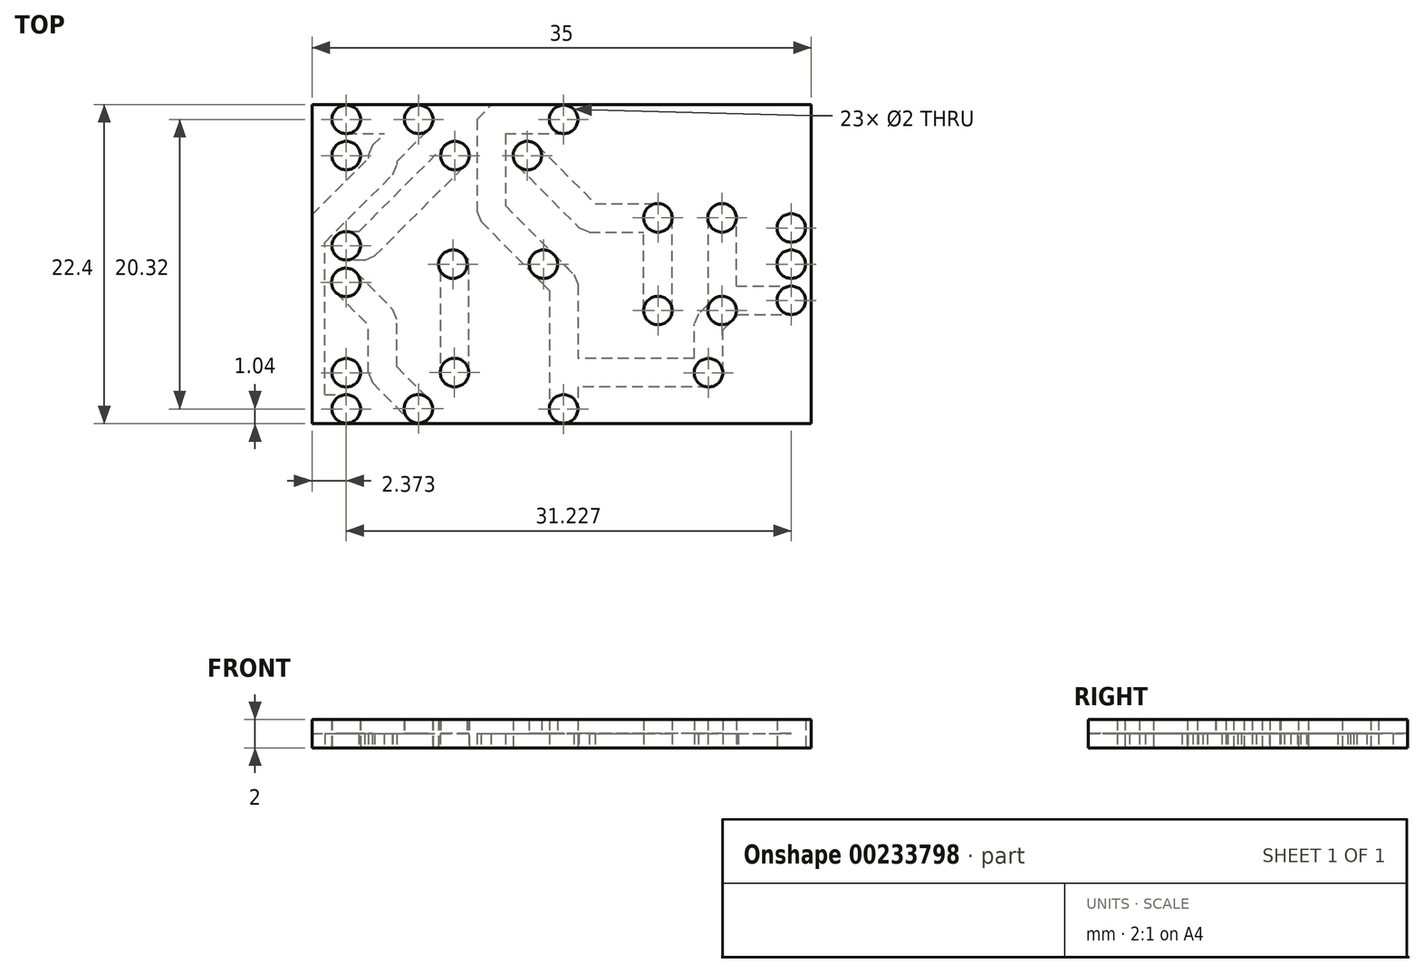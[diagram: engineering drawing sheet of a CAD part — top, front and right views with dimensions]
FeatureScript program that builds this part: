
annotation { "Feature Type Name" : "Feature", "Feature Type Description" : "" }
export const myFeature = defineFeature(function(context is Context, id is Id, definition is map)
    precondition{}
    {
        {
            var Q0;
            Q0=qCreatedBy(makeId("Top.planeOp"),FACE);
            var sketch = newSketch(context, id + "F0", { "sketchPlane" : qUnion([Q0])});
            skLineSegment(sketch, "E0.0", {"start": v(27.94, 0) * mm, "end": v(27.94, 15.24) * mm});
            skLineSegment(sketch, "E1", {"start": v(15.24, 15.24) * mm, "end": v(15.24, 17.78) * mm});
            skLineSegment(sketch, "E2.0", {"start": v(10.65, 6.33) * mm, "end": v(10.65, 8.91) * mm});
            skLineSegment(sketch, "E3.0", {"start": v(13.83, 6.33) * mm, "end": v(13.83, 8.91) * mm});
            skLineSegment(sketch, "E4.0", {"start": v(7.47, 6.33) * mm, "end": v(7.47, 8.91) * mm});
            skLineSegment(sketch, "E5.0", {"start": v(20.85, 6.33) * mm, "end": v(20.85, 8.91) * mm});
            skLineSegment(sketch, "E6.0", {"start": v(29.35, 6.33) * mm, "end": v(29.35, 8.91) * mm});
            skLineSegment(sketch, "E7.0", {"start": v(33.05, 6.33) * mm, "end": v(33.05, 8.91) * mm});
            skLineSegment(sketch, "E8.0", {"start": v(27.35, 6.33) * mm, "end": v(27.35, 8.91) * mm});
            skLineSegment(sketch, "E9", {"start": v(20.85, 7.62) * mm, "end": v(27.35, 7.62) * mm});
            skLineSegment(sketch, "E10", {"start": v(29.35, 7.62) * mm, "end": v(33.05, 7.62) * mm});
            skLineSegment(sketch, "E11", {"start": v(31.2, 7.62) * mm, "end": v(31.2, 10.16) * mm});
            skLineSegment(sketch, "E12", {"start": v(2.54, 15.24) * mm, "end": v(5.08, 17.78) * mm});
            skLineSegment(sketch, "E13", {"start": v(21.85, 4.37) * mm, "end": v(21.85, 10.87) * mm});
            skLineSegment(sketch, "E14", {"start": v(26.35, 10.87) * mm, "end": v(26.35, 4.37) * mm});
            skLineSegment(sketch, "E15", {"start": v(10.16, 17.78) * mm, "end": v(15.24, 17.78) * mm});
            skLineSegment(sketch, "E16", {"start": v(25.4, 0) * mm, "end": v(15.24, 0) * mm});
            skLineSegment(sketch, "E17", {"start": v(2.53, 0.01) * mm, "end": v(5.05, -2.53) * mm});
            skLineSegment(sketch, "E18", {"start": v(0, 15.24) * mm, "end": v(0, 8.91) * mm});
            skLineSegment(sketch, "E19", {"start": v(-2.56, -2.54) * mm, "end": v(0, -2.54) * mm});
            skLineSegment(sketch, "E20", {"start": v(0, 8.91) * mm, "end": v(0, 8.4) * mm});
            skLineSegment(sketch, "E21", {"start": v(2.54, 15.24) * mm, "end": v(2.54, 14.61) * mm});
            skLineSegment(sketch, "E22.trimOffspring", {"start": v(1.3, 8.91) * mm, "end": v(7.62, 15.24) * mm});
            skLineSegment(sketch, "E23", {"start": v(-0.03, 6.34) * mm, "end": v(2.53, 3.76) * mm});
            skLineSegment(sketch, "E24", {"start": v(2.53, 0.01) * mm, "end": v(2.53, 3.76) * mm});
            skLineSegment(sketch, "E25", {"start": v(12.7, 15.24) * mm, "end": v(17.03, 10.87) * mm});
            skLineSegment(sketch, "E26", {"start": v(17.03, 10.87) * mm, "end": v(21.85, 10.87) * mm});
            skLineSegment(sketch, "E27", {"start": v(15.24, 6.2) * mm, "end": v(15.24, -2.54) * mm});
            skLineSegment(sketch, "E28", {"start": v(25.4, 3.42) * mm, "end": v(27.06, 5.08) * mm});
            skLineSegment(sketch, "E29", {"start": v(27.06, 5.08) * mm, "end": v(31.2, 5.08) * mm});
            skLineSegment(sketch, "E30", {"start": v(1.3, 8.91) * mm, "end": v(0, 8.91) * mm});
            skLineSegment(sketch, "E31", {"start": v(-2.52, 0) * mm, "end": v(-2.52, 9.56) * mm});
            skLineSegment(sketch, "E32", {"start": v(25.4, 0) * mm, "end": v(25.4, 3.42) * mm});
            skLineSegment(sketch, "E33", {"start": v(0, 17.78) * mm, "end": v(5.08, 17.78) * mm});
            skLineSegment(sketch, "E34", {"start": v(-2.52, 9.56) * mm, "end": v(2.54, 14.61) * mm});
            skLineSegment(sketch, "E35", {"start": v(10.16, 11.32) * mm, "end": v(15.24, 6.2) * mm});
            skLineSegment(sketch, "E36", {"start": v(10.16, 17.78) * mm, "end": v(10.16, 11.32) * mm});
            skCircle(sketch, "E37", {"center": v(0, 17.78) * mm, "radius": 1 * mm});
            skCircle(sketch, "E38", {"center": v(5.08, 17.78) * mm, "radius": 1 * mm});
            skCircle(sketch, "E39", {"center": v(0, 15.24) * mm, "radius": 1 * mm});
            skCircle(sketch, "E40", {"center": v(7.62, 15.24) * mm, "radius": 1 * mm});
            skCircle(sketch, "E41", {"center": v(0, 8.91) * mm, "radius": 1 * mm});
            skCircle(sketch, "E42", {"center": v(-0.03, 6.34) * mm, "radius": 1 * mm});
            skCircle(sketch, "E43", {"center": v(0, 0) * mm, "radius": 1 * mm});
            skCircle(sketch, "E44", {"center": v(0, -2.54) * mm, "radius": 1 * mm});
            skCircle(sketch, "E45", {"center": v(5.05, -2.53) * mm, "radius": 1 * mm});
            skCircle(sketch, "E46", {"center": v(15.24, 17.78) * mm, "radius": 1 * mm});
            skCircle(sketch, "E47", {"center": v(12.7, 15.24) * mm, "radius": 1 * mm});
            skCircle(sketch, "E48", {"center": v(21.85, 10.87) * mm, "radius": 1 * mm});
            skCircle(sketch, "E49", {"center": v(21.85, 4.37) * mm, "radius": 1 * mm});
            skCircle(sketch, "E50", {"center": v(13.83, 7.62) * mm, "radius": 1 * mm});
            skCircle(sketch, "E51", {"center": v(26.35, 10.87) * mm, "radius": 1 * mm});
            skCircle(sketch, "E52", {"center": v(26.35, 4.37) * mm, "radius": 1 * mm});
            skCircle(sketch, "E53", {"center": v(25.4, 0) * mm, "radius": 1 * mm});
            skCircle(sketch, "E54", {"center": v(15.24, -2.54) * mm, "radius": 1 * mm});
            skCircle(sketch, "E55", {"center": v(31.2, 5.08) * mm, "radius": 1 * mm});
            skCircle(sketch, "E56", {"center": v(31.2, 7.62) * mm, "radius": 1 * mm});
            skCircle(sketch, "E57", {"center": v(31.2, 10.16) * mm, "radius": 1 * mm});
            skLineSegment(sketch, "E58.0", {"start": v(0, 16.78) * mm, "end": v(5.08, 16.78) * mm});
            skLineSegment(sketch, "E59.0", {"start": v(0, 18.78) * mm, "end": v(5.08, 18.78) * mm});
            skLineSegment(sketch, "E60.0", {"start": v(3.25, 14.53) * mm, "end": v(5.79, 17.07) * mm});
            skLineSegment(sketch, "E61.0", {"start": v(1.83, 15.95) * mm, "end": v(4.37, 18.49) * mm});
            skLineSegment(sketch, "E62.0", {"start": v(1.54, 15.24) * mm, "end": v(1.54, 14.61) * mm});
            skLineSegment(sketch, "E63.0", {"start": v(3.54, 15.24) * mm, "end": v(3.54, 14.61) * mm});
            skLineSegment(sketch, "E64.0", {"start": v(-1.81, 8.85) * mm, "end": v(3.25, 13.9) * mm});
            skLineSegment(sketch, "E65.0", {"start": v(-3.23, 10.26) * mm, "end": v(1.83, 15.32) * mm});
            skLineSegment(sketch, "E66.0", {"start": v(-1.52, 0) * mm, "end": v(-1.52, 9.56) * mm});
            skLineSegment(sketch, "E67.0", {"start": v(2, 8.2) * mm, "end": v(8.33, 14.53) * mm});
            skLineSegment(sketch, "E68.0", {"start": v(0.58, 9.62) * mm, "end": v(6.91, 15.95) * mm});
            skLineSegment(sketch, "E69.0", {"start": v(1.3, 7.9) * mm, "end": v(0, 7.9) * mm});
            skLineSegment(sketch, "E70.0", {"start": v(1.3, 9.91) * mm, "end": v(0, 9.91) * mm});
            skLineSegment(sketch, "E71.0", {"start": v(3.55, 0.98) * mm, "end": v(1.03, 3.52) * mm});
            skLineSegment(sketch, "E72", {"start": v(0, -2.54) * mm, "end": v(-2.52, -2.54) * mm});
            skLineSegment(sketch, "E73", {"start": v(-2.52, -2.54) * mm, "end": v(-2.52, 0) * mm});
            skLineSegment(sketch, "E74.0", {"start": v(-2.52, -3.54) * mm, "end": v(0, -3.54) * mm});
            skLineSegment(sketch, "E75.0", {"start": v(-2.56, -1.54) * mm, "end": v(0, -1.54) * mm});
            skLineSegment(sketch, "E76", {"start": v(-1.52, 0) * mm, "end": v(-1.52, -1.54) * mm});
            skLineSegment(sketch, "E77", {"start": v(-2.52, -2.54) * mm, "end": v(-2.52, -3.54) * mm});
            skLineSegment(sketch, "E78.0", {"start": v(-0.74, 5.64) * mm, "end": v(1.82, 3.06) * mm});
            skLineSegment(sketch, "E79.0", {"start": v(0.68, 7.05) * mm, "end": v(3.24, 4.47) * mm});
            skLineSegment(sketch, "E80.0", {"start": v(3.53, 0.01) * mm, "end": v(3.53, 3.77) * mm});
            skLineSegment(sketch, "E81.0", {"start": v(1.53, 0) * mm, "end": v(1.53, 3.76) * mm});
            skCircle(sketch, "E82", {"center": v(7.6, 0.01) * mm, "radius": 1 * mm});
            skCircle(sketch, "E83", {"center": v(7.47, 7.62) * mm, "radius": 1 * mm});
            skLineSegment(sketch, "E84.0", {"start": v(1.82, -0.7) * mm, "end": v(4.34, -3.23) * mm});
            skLineSegment(sketch, "E85.0", {"start": v(3.24, 0.72) * mm, "end": v(5.76, -1.82) * mm});
            skLineSegment(sketch, "E86", {"start": v(6.6, 7.15) * mm, "end": v(6.6, 0.01) * mm});
            skLineSegment(sketch, "E87", {"start": v(7.47, 7.62) * mm, "end": v(5.78, 5.92) * mm});
            skLineSegment(sketch, "E88", {"start": v(5.78, 5.92) * mm, "end": v(8.47, 8.61) * mm});
            skLineSegment(sketch, "E89", {"start": v(8.18, 8.33) * mm, "end": v(8.9, 7.62) * mm});
            skLineSegment(sketch, "E90", {"start": v(8.6, 0) * mm, "end": v(8.6, 7.92) * mm});
            skLineSegment(sketch, "E91.0", {"start": v(10.16, 16.78) * mm, "end": v(15.24, 16.78) * mm});
            skLineSegment(sketch, "E92.0", {"start": v(10.16, 18.78) * mm, "end": v(15.24, 18.78) * mm});
            skLineSegment(sketch, "E93.0", {"start": v(11.16, 17.78) * mm, "end": v(11.16, 11.32) * mm});
            skLineSegment(sketch, "E94.0", {"start": v(9.16, 17.78) * mm, "end": v(9.16, 11.32) * mm});
            skLineSegment(sketch, "E95.0", {"start": v(9.45, 10.61) * mm, "end": v(14.53, 5.49) * mm});
            skLineSegment(sketch, "E96.0", {"start": v(10.87, 12.02) * mm, "end": v(15.95, 6.9) * mm});
            skLineSegment(sketch, "E97.0", {"start": v(13.4, 15.94) * mm, "end": v(17.74, 11.57) * mm});
            skLineSegment(sketch, "E98.0", {"start": v(12, 14.54) * mm, "end": v(16.32, 10.17) * mm});
            skLineSegment(sketch, "E99.0", {"start": v(17.03, 9.87) * mm, "end": v(21.85, 9.87) * mm});
            skLineSegment(sketch, "E100.0", {"start": v(17.03, 11.87) * mm, "end": v(21.85, 11.87) * mm});
            skLineSegment(sketch, "E101.0", {"start": v(14.24, 6.2) * mm, "end": v(14.24, -2.54) * mm});
            skLineSegment(sketch, "E102.0", {"start": v(16.24, 6.2) * mm, "end": v(16.24, -2.54) * mm});
            skLineSegment(sketch, "E103.0", {"start": v(22.85, 4.37) * mm, "end": v(22.85, 10.87) * mm});
            skLineSegment(sketch, "E104.0", {"start": v(20.85, 4.37) * mm, "end": v(20.85, 10.87) * mm});
            skLineSegment(sketch, "E105.0", {"start": v(25.35, 10.87) * mm, "end": v(25.35, 4.37) * mm});
            skLineSegment(sketch, "E106.0", {"start": v(27.35, 10.87) * mm, "end": v(27.35, 4.37) * mm});
            skLineSegment(sketch, "E107.0", {"start": v(27.06, 4.08) * mm, "end": v(31.2, 4.08) * mm});
            skLineSegment(sketch, "E108.0", {"start": v(27.06, 6.08) * mm, "end": v(31.2, 6.08) * mm});
            skLineSegment(sketch, "E109.0", {"start": v(26.4, 0) * mm, "end": v(26.4, 3.42) * mm});
            skLineSegment(sketch, "E110.0", {"start": v(24.4, 0) * mm, "end": v(24.4, 3.42) * mm});
            skLineSegment(sketch, "E111.0", {"start": v(25.64, 5.08) * mm, "end": v(24.7, 4.13) * mm});
            skLineSegment(sketch, "E112.0", {"start": v(26.1, 2.71) * mm, "end": v(27.77, 4.37) * mm});
            skLineSegment(sketch, "E113", {"start": v(24.7, 4.13) * mm, "end": v(24.4, 3.42) * mm});
            skLineSegment(sketch, "E114", {"start": v(17.03, 9.87) * mm, "end": v(16.32, 10.17) * mm});
            skLineSegment(sketch, "E115", {"start": v(15.95, 6.9) * mm, "end": v(16.24, 6.2) * mm});
            skLineSegment(sketch, "E116", {"start": v(9.16, 11.32) * mm, "end": v(9.45, 10.61) * mm});
            skLineSegment(sketch, "E117", {"start": v(9.16, 17.78) * mm, "end": v(10.16, 18.78) * mm});
            skLineSegment(sketch, "E118", {"start": v(3.24, 4.47) * mm, "end": v(3.53, 3.77) * mm});
            skLineSegment(sketch, "E119", {"start": v(1.53, 0) * mm, "end": v(1.82, -0.7) * mm});
            skLineSegment(sketch, "E120", {"start": v(1.3, 7.9) * mm, "end": v(2, 8.2) * mm});
            skLineSegment(sketch, "E121", {"start": v(3.25, 13.9) * mm, "end": v(3.54, 14.61) * mm});
            skLineSegment(sketch, "E122", {"start": v(1.83, 15.95) * mm, "end": v(1.54, 15.24) * mm});
            skLineSegment(sketch, "E123", {"start": v(-2.52, 9.56) * mm, "end": v(-2.52, 10.97) * mm});
            skLineSegment(sketch, "E124.0", {"start": v(25.4, 1) * mm, "end": v(15.24, 1) * mm});
            skLineSegment(sketch, "E125.0", {"start": v(25.4, -1) * mm, "end": v(15.24, -1) * mm});
            skSolve(sketch);
        }
        {
            var Q0;
            Q0=qCreatedBy(makeId("Top.planeOp"),FACE);
            var sketch = newSketch(context, id + "F1", { "sketchPlane" : qUnion([Q0])});
            skLineSegment(sketch, "E126", {"start": v(-2.4, -4.38) * mm, "end": v(-2.4, 19.62) * mm});
            skLineSegment(sketch, "E127", {"start": v(-2.4, 19.62) * mm, "end": v(32.6, 19.62) * mm});
            skLineSegment(sketch, "E128", {"start": v(32.6, 19.62) * mm, "end": v(32.6, -4.38) * mm});
            skLineSegment(sketch, "E129", {"start": v(32.6, -4.38) * mm, "end": v(-2.4, -4.38) * mm});
            skLineSegment(sketch, "E130.0", {"start": v(32.6, -3.58) * mm, "end": v(-2.4, -3.58) * mm});
            skLineSegment(sketch, "E131.0", {"start": v(-2.4, 18.82) * mm, "end": v(32.6, 18.82) * mm});
            skSolve(sketch);
        }
        {
            var Q0;
            {var subQ0=sQuery(id+"F1.wireOp",EDGE,"E130.0");Q0=makeQuery(id+"F1.imprint","IMPRINT",FACE,{"disambiguationData":[TD([[makeQuery(id+"F1.imprint","IMPRINT",EDGE,{"derivedFrom":subQ0}),-1.0]])]});}
            extrude(context, id + "F2", {"entities" : qUnion([Q0]), "depth" : 2 * mm});
        }
        {
            var Q0;
            Q0 = qSketchRegion(id + "F0", true);
            var Q1;
            {var subQ0=sQuery(id+"F0.wireOp",EDGE,"E61.0");var subQ1=sQuery(id+"F0.wireOp",EDGE,"E33");var subQ2=makeQuery(id+"F0.imprint","INTERSECT",VERTEX,{"derivedFrom":[subQ1,subQ0]});Q1=makeQuery(id+"F0.imprint","IMPRINT",FACE,{"disambiguationData":[TD([[makeQuery(id+"F0.imprint","IMPRINT",EDGE,{"disambiguationData":[TD([[subQ2,-1.0]])],"derivedFrom":subQ1}),1.0]])]});}
            var Q2;
            {var subQ0=sQuery(id+"F0.wireOp",EDGE,"E33");var subQ1=sQuery(id+"F0.wireOp",EDGE,"E12");var subQ2=makeQuery(id+"F0.imprint","INTERSECT",VERTEX,{"derivedFrom":[subQ1,subQ0]});Q2=makeQuery(id+"F0.imprint","IMPRINT",FACE,{"disambiguationData":[TD([[makeQuery(id+"F0.imprint","IMPRINT",EDGE,{"disambiguationData":[TD([[subQ2,1.0]])],"derivedFrom":subQ1}),1.0]])]});}
            var Q3;
            {var subQ0=sQuery(id+"F0.wireOp",EDGE,"E58.0");var subQ1=sQuery(id+"F0.wireOp",EDGE,"E12");var subQ2=makeQuery(id+"F0.imprint","INTERSECT",VERTEX,{"derivedFrom":[subQ1,subQ0]});Q3=makeQuery(id+"F0.imprint","IMPRINT",FACE,{"disambiguationData":[TD([[makeQuery(id+"F0.imprint","IMPRINT",EDGE,{"disambiguationData":[TD([[subQ2,-1.0]])],"derivedFrom":subQ1}),-1.0]])]});}
            var Q4;
            {var subQ0=sQuery(id+"F0.wireOp",EDGE,"E83");var subQ1=sQuery(id+"F0.wireOp",EDGE,"E4.0");var subQ2=makeQuery(id+"F0.imprint","INTERSECT",VERTEX,{"disambiguationData":[OD(1.0)],"derivedFrom":[subQ1,subQ0]});Q4=makeQuery(id+"F0.imprint","IMPRINT",FACE,{"disambiguationData":[TD([[makeQuery(id+"F0.imprint","IMPRINT",EDGE,{"disambiguationData":[TD([[subQ2,-1.0]])],"derivedFrom":subQ1}),1.0]])]});}
            var Q5;
            {var subQ0=sQuery(id+"F0.wireOp",EDGE,"E50");var subQ1=sQuery(id+"F0.wireOp",EDGE,"E3.0");var subQ2=makeQuery(id+"F0.imprint","INTERSECT",VERTEX,{"disambiguationData":[OD(1.0)],"derivedFrom":[subQ1,subQ0]});Q5=makeQuery(id+"F0.imprint","IMPRINT",FACE,{"disambiguationData":[TD([[makeQuery(id+"F0.imprint","IMPRINT",EDGE,{"disambiguationData":[TD([[subQ2,1.0]])],"derivedFrom":subQ1}),1.0]])]});}
            var Q6;
            {var subQ0=sQuery(id+"F0.wireOp",EDGE,"E50");var subQ1=sQuery(id+"F0.wireOp",EDGE,"E3.0");var subQ2=makeQuery(id+"F0.imprint","INTERSECT",VERTEX,{"disambiguationData":[OD(0.0)],"derivedFrom":[subQ1,subQ0]});Q6=makeQuery(id+"F0.imprint","IMPRINT",FACE,{"disambiguationData":[TD([[makeQuery(id+"F0.imprint","IMPRINT",EDGE,{"disambiguationData":[TD([[subQ2,-1.0]])],"derivedFrom":subQ1}),-1.0]])]});}
            var Q7;
            {var subQ0=sQuery(id+"F0.wireOp",EDGE,"E26");var subQ1=sQuery(id+"F0.wireOp",EDGE,"E13");var subQ2=makeQuery(id+"F0.imprint","INTERSECT",VERTEX,{"derivedFrom":[subQ1,subQ0]});Q7=makeQuery(id+"F0.imprint","IMPRINT",FACE,{"disambiguationData":[TD([[makeQuery(id+"F0.imprint","IMPRINT",EDGE,{"disambiguationData":[TD([[subQ2,1.0]])],"derivedFrom":subQ1}),1.0]])]});}
            var Q8;
            {var subQ2=sQuery(id+"F0.wireOp",EDGE,"E14");var subQ4=sQuery(id+"F0.wireOp",EDGE,"E28");var subQ5=makeQuery(id+"F0.imprint","INTERSECT",VERTEX,{"derivedFrom":[subQ2,subQ4]});Q8=makeQuery(id+"F0.imprint","IMPRINT",FACE,{"disambiguationData":[TD([[makeQuery(id+"F0.imprint","IMPRINT",EDGE,{"disambiguationData":[TD([[subQ5,1.0]])],"derivedFrom":subQ2}),-1.0]])]});}
            var Q9;
            {var subQ0=sQuery(id+"F0.wireOp",EDGE,"E28");var subQ1=sQuery(id+"F0.wireOp",EDGE,"E14");var subQ2=makeQuery(id+"F0.imprint","INTERSECT",VERTEX,{"derivedFrom":[subQ1,subQ0]});Q9=makeQuery(id+"F0.imprint","IMPRINT",FACE,{"disambiguationData":[TD([[makeQuery(id+"F0.imprint","IMPRINT",EDGE,{"disambiguationData":[TD([[subQ2,1.0]])],"derivedFrom":subQ1}),1.0]])]});}
            var Q10;
            {var subQ0=sQuery(id+"F0.wireOp",EDGE,"E29");var subQ1=sQuery(id+"F0.wireOp",EDGE,"E28");var subQ2=makeQuery(id+"F0.imprint","INTERSECT",VERTEX,{"derivedFrom":[subQ1,subQ0]});Q10=makeQuery(id+"F0.imprint","IMPRINT",FACE,{"disambiguationData":[TD([[makeQuery(id+"F0.imprint","IMPRINT",EDGE,{"disambiguationData":[TD([[subQ2,1.0]])],"derivedFrom":subQ1}),-1.0]])]});}
            extrude(context, id + "F3", {"entities" : qUnion([Q0, Q1, Q2, Q3, Q4, Q5, Q6, Q7, Q8, Q9, Q10]), "operationType" : NewBodyOperationType.REMOVE, "depth" : 1 * mm});
        }
        {
            var Q0;
            {var subQ0=sQuery(id+"F0.wireOp",EDGE,"E15");var subQ1=sQuery(id+"F0.wireOp",EDGE,"E1");var subQ2=makeQuery(id+"F0.imprint","INTERSECT",VERTEX,{"derivedFrom":[subQ1,subQ0]});Q0=makeQuery(id+"F0.imprint","IMPRINT",FACE,{"disambiguationData":[TD([[makeQuery(id+"F0.imprint","IMPRINT",EDGE,{"disambiguationData":[TD([[subQ2,1.0]])],"derivedFrom":subQ0}),1.0]])]});}
            var Q1;
            {var subQ0=sQuery(id+"F0.wireOp",EDGE,"E15");var subQ1=sQuery(id+"F0.wireOp",EDGE,"E1");var subQ2=makeQuery(id+"F0.imprint","INTERSECT",VERTEX,{"derivedFrom":[subQ1,subQ0]});Q1=makeQuery(id+"F0.imprint","IMPRINT",FACE,{"disambiguationData":[TD([[makeQuery(id+"F0.imprint","IMPRINT",EDGE,{"disambiguationData":[TD([[subQ2,1.0]])],"derivedFrom":subQ0}),-1.0]])]});}
            var Q2;
            {var subQ0=sQuery(id+"F0.wireOp",EDGE,"E47");var subQ1=makeQuery(id+"F0.imprint","INTERSECT",VERTEX,{"derivedFrom":[subQ0,sQuery(id+"F0.wireOp",EDGE,"E97.0")]});Q2=makeQuery(id+"F0.imprint","IMPRINT",FACE,{"disambiguationData":[TD([[makeQuery(id+"F0.imprint","IMPRINT",EDGE,{"disambiguationData":[TD([[subQ1,-1.0]])],"derivedFrom":subQ0}),1.0]])]});}
            var Q3;
            {var subQ0=sQuery(id+"F0.wireOp",EDGE,"E50");var subQ1=sQuery(id+"F0.wireOp",EDGE,"E3.0");var subQ2=makeQuery(id+"F0.imprint","INTERSECT",VERTEX,{"disambiguationData":[OD(1.0)],"derivedFrom":[subQ1,subQ0]});Q3=makeQuery(id+"F0.imprint","IMPRINT",FACE,{"disambiguationData":[TD([[makeQuery(id+"F0.imprint","IMPRINT",EDGE,{"disambiguationData":[TD([[subQ2,1.0]])],"derivedFrom":subQ1}),-1.0]])]});}
            var Q4;
            {var subQ0=sQuery(id+"F0.wireOp",EDGE,"E50");var subQ1=sQuery(id+"F0.wireOp",EDGE,"E3.0");var subQ2=makeQuery(id+"F0.imprint","INTERSECT",VERTEX,{"disambiguationData":[OD(1.0)],"derivedFrom":[subQ1,subQ0]});Q4=makeQuery(id+"F0.imprint","IMPRINT",FACE,{"disambiguationData":[TD([[makeQuery(id+"F0.imprint","IMPRINT",EDGE,{"disambiguationData":[TD([[subQ2,1.0]])],"derivedFrom":subQ1}),1.0]])]});}
            var Q5;
            {var subQ0=sQuery(id+"F0.wireOp",EDGE,"E50");var subQ1=sQuery(id+"F0.wireOp",EDGE,"E3.0");var subQ2=makeQuery(id+"F0.imprint","INTERSECT",VERTEX,{"disambiguationData":[OD(0.0)],"derivedFrom":[subQ1,subQ0]});Q5=makeQuery(id+"F0.imprint","IMPRINT",FACE,{"disambiguationData":[TD([[makeQuery(id+"F0.imprint","IMPRINT",EDGE,{"disambiguationData":[TD([[subQ2,-1.0]])],"derivedFrom":subQ1}),-1.0]])]});}
            var Q6;
            {var subQ0=sQuery(id+"F0.wireOp",EDGE,"E50");var subQ1=sQuery(id+"F0.wireOp",EDGE,"E3.0");var subQ2=makeQuery(id+"F0.imprint","INTERSECT",VERTEX,{"disambiguationData":[OD(0.0)],"derivedFrom":[subQ1,subQ0]});Q6=makeQuery(id+"F0.imprint","IMPRINT",FACE,{"disambiguationData":[TD([[makeQuery(id+"F0.imprint","IMPRINT",EDGE,{"disambiguationData":[TD([[subQ2,-1.0]])],"derivedFrom":subQ1}),1.0]])]});}
            var Q7;
            {var subQ0=sQuery(id+"F0.wireOp",EDGE,"E83");var subQ1=sQuery(id+"F0.wireOp",EDGE,"E4.0");var subQ2=makeQuery(id+"F0.imprint","INTERSECT",VERTEX,{"disambiguationData":[OD(1.0)],"derivedFrom":[subQ1,subQ0]});Q7=makeQuery(id+"F0.imprint","IMPRINT",FACE,{"disambiguationData":[TD([[makeQuery(id+"F0.imprint","IMPRINT",EDGE,{"disambiguationData":[TD([[subQ2,-1.0]])],"derivedFrom":subQ1}),-1.0]])]});}
            var Q8;
            {var subQ0=sQuery(id+"F0.wireOp",EDGE,"E83");var subQ1=sQuery(id+"F0.wireOp",EDGE,"E4.0");var subQ2=makeQuery(id+"F0.imprint","INTERSECT",VERTEX,{"disambiguationData":[OD(0.0)],"derivedFrom":[subQ1,subQ0]});Q8=makeQuery(id+"F0.imprint","IMPRINT",FACE,{"disambiguationData":[TD([[makeQuery(id+"F0.imprint","IMPRINT",EDGE,{"disambiguationData":[TD([[subQ2,1.0]])],"derivedFrom":subQ1}),-1.0]])]});}
            var Q9;
            {var subQ0=sQuery(id+"F0.wireOp",EDGE,"E83");var subQ1=sQuery(id+"F0.wireOp",EDGE,"E4.0");var subQ2=makeQuery(id+"F0.imprint","INTERSECT",VERTEX,{"disambiguationData":[OD(0.0)],"derivedFrom":[subQ1,subQ0]});Q9=makeQuery(id+"F0.imprint","IMPRINT",FACE,{"disambiguationData":[TD([[makeQuery(id+"F0.imprint","IMPRINT",EDGE,{"disambiguationData":[TD([[subQ2,1.0]])],"derivedFrom":subQ1}),1.0]])]});}
            var Q10;
            {var subQ0=sQuery(id+"F0.wireOp",EDGE,"E83");var subQ1=sQuery(id+"F0.wireOp",EDGE,"E4.0");var subQ2=makeQuery(id+"F0.imprint","INTERSECT",VERTEX,{"disambiguationData":[OD(1.0)],"derivedFrom":[subQ1,subQ0]});Q10=makeQuery(id+"F0.imprint","IMPRINT",FACE,{"disambiguationData":[TD([[makeQuery(id+"F0.imprint","IMPRINT",EDGE,{"disambiguationData":[TD([[subQ2,-1.0]])],"derivedFrom":subQ1}),1.0]])]});}
            var Q11;
            {var subQ0=sQuery(id+"F0.wireOp",EDGE,"E82");var subQ1=makeQuery(id+"F0.imprint","INTERSECT",VERTEX,{"derivedFrom":[subQ0,sQuery(id+"F0.wireOp",EDGE,"E86")]});Q11=makeQuery(id+"F0.imprint","IMPRINT",FACE,{"disambiguationData":[TD([[makeQuery(id+"F0.imprint","IMPRINT",EDGE,{"disambiguationData":[TD([[subQ1,1.0]])],"derivedFrom":subQ0}),1.0]])]});}
            var Q12;
            {var subQ0=sQuery(id+"F0.wireOp",EDGE,"E42");var subQ1=makeQuery(id+"F0.imprint","INTERSECT",VERTEX,{"derivedFrom":[subQ0,sQuery(id+"F0.wireOp",EDGE,"E78.0")]});Q12=makeQuery(id+"F0.imprint","IMPRINT",FACE,{"disambiguationData":[TD([[makeQuery(id+"F0.imprint","IMPRINT",EDGE,{"disambiguationData":[TD([[subQ1,1.0]])],"derivedFrom":subQ0}),1.0]])]});}
            var Q13;
            {var subQ0=sQuery(id+"F0.wireOp",EDGE,"E30");var subQ1=sQuery(id+"F0.wireOp",EDGE,"E18");var subQ2=makeQuery(id+"F0.imprint","INTERSECT",VERTEX,{"derivedFrom":[subQ1,subQ0]});Q13=makeQuery(id+"F0.imprint","IMPRINT",FACE,{"disambiguationData":[TD([[makeQuery(id+"F0.imprint","IMPRINT",EDGE,{"disambiguationData":[TD([[subQ2,1.0]])],"derivedFrom":subQ0}),1.0]])]});}
            var Q14;
            {var subQ0=sQuery(id+"F0.wireOp",EDGE,"E30");var subQ1=sQuery(id+"F0.wireOp",EDGE,"E18");var subQ2=makeQuery(id+"F0.imprint","INTERSECT",VERTEX,{"derivedFrom":[subQ1,subQ0]});Q14=makeQuery(id+"F0.imprint","IMPRINT",FACE,{"disambiguationData":[TD([[makeQuery(id+"F0.imprint","IMPRINT",EDGE,{"disambiguationData":[TD([[subQ2,1.0]])],"derivedFrom":subQ0}),-1.0]])]});}
            var Q15;
            {var subQ0=sQuery(id+"F0.wireOp",EDGE,"E40");var subQ1=makeQuery(id+"F0.imprint","INTERSECT",VERTEX,{"derivedFrom":[subQ0,sQuery(id+"F0.wireOp",EDGE,"E68.0")]});Q15=makeQuery(id+"F0.imprint","IMPRINT",FACE,{"disambiguationData":[TD([[makeQuery(id+"F0.imprint","IMPRINT",EDGE,{"disambiguationData":[TD([[subQ1,-1.0]])],"derivedFrom":subQ0}),1.0]])]});}
            var Q16;
            {var subQ0=sQuery(id+"F0.wireOp",EDGE,"E33");var subQ1=sQuery(id+"F0.wireOp",EDGE,"E12");var subQ2=makeQuery(id+"F0.imprint","INTERSECT",VERTEX,{"derivedFrom":[subQ1,subQ0]});Q16=makeQuery(id+"F0.imprint","IMPRINT",FACE,{"disambiguationData":[TD([[makeQuery(id+"F0.imprint","IMPRINT",EDGE,{"disambiguationData":[TD([[subQ2,1.0]])],"derivedFrom":subQ1}),-1.0]])]});}
            var Q17;
            {var subQ0=sQuery(id+"F0.wireOp",EDGE,"E33");var subQ1=sQuery(id+"F0.wireOp",EDGE,"E12");var subQ2=makeQuery(id+"F0.imprint","INTERSECT",VERTEX,{"derivedFrom":[subQ1,subQ0]});Q17=makeQuery(id+"F0.imprint","IMPRINT",FACE,{"disambiguationData":[TD([[makeQuery(id+"F0.imprint","IMPRINT",EDGE,{"disambiguationData":[TD([[subQ2,1.0]])],"derivedFrom":subQ1}),1.0]])]});}
            var Q18;
            {var subQ0=sQuery(id+"F0.wireOp",EDGE,"E37");var subQ1=makeQuery(id+"F0.imprint","INTERSECT",VERTEX,{"derivedFrom":[subQ0,sQuery(id+"F0.wireOp",EDGE,"E59.0")]});Q18=makeQuery(id+"F0.imprint","IMPRINT",FACE,{"disambiguationData":[TD([[makeQuery(id+"F0.imprint","IMPRINT",EDGE,{"disambiguationData":[TD([[subQ1,1.0]])],"derivedFrom":subQ0}),1.0]])]});}
            var Q19;
            Q19=makeQuery(id+"F0.imprint","IMPRINT",FACE,{"disambiguationData":[TD([[makeQuery(id+"F0.imprint","IMPRINT",EDGE,{"derivedFrom":sQuery(id+"F0.wireOp",EDGE,"E39")}),1.0]])]});
            var Q20;
            Q20=makeQuery(id+"F0.imprint","IMPRINT",FACE,{"disambiguationData":[TD([[makeQuery(id+"F0.imprint","IMPRINT",EDGE,{"derivedFrom":sQuery(id+"F0.wireOp",EDGE,"E43")}),1.0]])]});
            var Q21;
            {var subQ0=sQuery(id+"F0.wireOp",EDGE,"E44");var subQ1=makeQuery(id+"F0.imprint","INTERSECT",VERTEX,{"derivedFrom":[subQ0,sQuery(id+"F0.wireOp",EDGE,"E75.0")]});Q21=makeQuery(id+"F0.imprint","IMPRINT",FACE,{"disambiguationData":[TD([[makeQuery(id+"F0.imprint","IMPRINT",EDGE,{"disambiguationData":[TD([[subQ1,-1.0]])],"derivedFrom":subQ0}),1.0]])]});}
            var Q22;
            {var subQ0=sQuery(id+"F0.wireOp",EDGE,"E45");var subQ1=makeQuery(id+"F0.imprint","INTERSECT",VERTEX,{"derivedFrom":[subQ0,sQuery(id+"F0.wireOp",EDGE,"E85.0")]});Q22=makeQuery(id+"F0.imprint","IMPRINT",FACE,{"disambiguationData":[TD([[makeQuery(id+"F0.imprint","IMPRINT",EDGE,{"disambiguationData":[TD([[subQ1,-1.0]])],"derivedFrom":subQ0}),1.0]])]});}
            var Q23;
            {var subQ0=sQuery(id+"F0.wireOp",EDGE,"E54");var subQ1=makeQuery(id+"F0.imprint","INTERSECT",VERTEX,{"derivedFrom":[subQ0,sQuery(id+"F0.wireOp",EDGE,"E102.0")]});Q23=makeQuery(id+"F0.imprint","IMPRINT",FACE,{"disambiguationData":[TD([[makeQuery(id+"F0.imprint","IMPRINT",EDGE,{"disambiguationData":[TD([[subQ1,-1.0]])],"derivedFrom":subQ0}),1.0]])]});}
            var Q24;
            {var subQ0=sQuery(id+"F0.wireOp",EDGE,"E49");var subQ1=makeQuery(id+"F0.imprint","INTERSECT",VERTEX,{"derivedFrom":[subQ0,sQuery(id+"F0.wireOp",EDGE,"E103.0")]});Q24=makeQuery(id+"F0.imprint","IMPRINT",FACE,{"disambiguationData":[TD([[makeQuery(id+"F0.imprint","IMPRINT",EDGE,{"disambiguationData":[TD([[subQ1,-1.0]])],"derivedFrom":subQ0}),1.0]])]});}
            var Q25;
            {var subQ0=sQuery(id+"F0.wireOp",EDGE,"E48");var subQ1=makeQuery(id+"F0.imprint","INTERSECT",VERTEX,{"derivedFrom":[subQ0,sQuery(id+"F0.wireOp",EDGE,"E100.0")]});Q25=makeQuery(id+"F0.imprint","IMPRINT",FACE,{"disambiguationData":[TD([[makeQuery(id+"F0.imprint","IMPRINT",EDGE,{"disambiguationData":[TD([[subQ1,1.0]])],"derivedFrom":subQ0}),1.0]])]});}
            var Q26;
            {var subQ0=sQuery(id+"F0.wireOp",EDGE,"E26");var subQ1=sQuery(id+"F0.wireOp",EDGE,"E13");var subQ2=makeQuery(id+"F0.imprint","INTERSECT",VERTEX,{"derivedFrom":[subQ1,subQ0]});Q26=makeQuery(id+"F0.imprint","IMPRINT",FACE,{"disambiguationData":[TD([[makeQuery(id+"F0.imprint","IMPRINT",EDGE,{"disambiguationData":[TD([[subQ2,1.0]])],"derivedFrom":subQ1}),1.0]])]});}
            var Q27;
            {var subQ0=sQuery(id+"F0.wireOp",EDGE,"E51");var subQ1=makeQuery(id+"F0.imprint","INTERSECT",VERTEX,{"derivedFrom":[subQ0,sQuery(id+"F0.wireOp",EDGE,"E105.0")]});Q27=makeQuery(id+"F0.imprint","IMPRINT",FACE,{"disambiguationData":[TD([[makeQuery(id+"F0.imprint","IMPRINT",EDGE,{"disambiguationData":[TD([[subQ1,1.0]])],"derivedFrom":subQ0}),1.0]])]});}
            var Q28;
            Q28=makeQuery(id+"F0.imprint","IMPRINT",FACE,{"disambiguationData":[TD([[makeQuery(id+"F0.imprint","IMPRINT",EDGE,{"derivedFrom":sQuery(id+"F0.wireOp",EDGE,"E57")}),1.0]])]});
            var Q29;
            {var subQ0=sQuery(id+"F0.wireOp",EDGE,"E11");var subQ1=sQuery(id+"F0.wireOp",EDGE,"E10");var subQ2=makeQuery(id+"F0.imprint","INTERSECT",VERTEX,{"derivedFrom":[subQ1,subQ0]});Q29=makeQuery(id+"F0.imprint","IMPRINT",FACE,{"disambiguationData":[TD([[makeQuery(id+"F0.imprint","IMPRINT",EDGE,{"disambiguationData":[TD([[subQ2,-1.0]])],"derivedFrom":subQ1}),1.0]])]});}
            var Q30;
            {var subQ0=sQuery(id+"F0.wireOp",EDGE,"E10");var subQ1=makeQuery(id+"F0.imprint","INTERSECT",VERTEX,{"derivedFrom":[subQ0,sQuery(id+"F0.wireOp",EDGE,"E11")]});Q30=makeQuery(id+"F0.imprint","IMPRINT",FACE,{"disambiguationData":[TD([[makeQuery(id+"F0.imprint","IMPRINT",EDGE,{"disambiguationData":[TD([[subQ1,1.0]])],"derivedFrom":subQ0}),-1.0]])]});}
            var Q31;
            {var subQ0=sQuery(id+"F0.wireOp",EDGE,"E11");var subQ1=sQuery(id+"F0.wireOp",EDGE,"E10");var subQ2=makeQuery(id+"F0.imprint","INTERSECT",VERTEX,{"derivedFrom":[subQ1,subQ0]});Q31=makeQuery(id+"F0.imprint","IMPRINT",FACE,{"disambiguationData":[TD([[makeQuery(id+"F0.imprint","IMPRINT",EDGE,{"disambiguationData":[TD([[subQ2,1.0]])],"derivedFrom":subQ1}),1.0]])]});}
            var Q32;
            {var subQ0=sQuery(id+"F0.wireOp",EDGE,"E55");var subQ1=makeQuery(id+"F0.imprint","INTERSECT",VERTEX,{"derivedFrom":[subQ0,sQuery(id+"F0.wireOp",EDGE,"E108.0")]});Q32=makeQuery(id+"F0.imprint","IMPRINT",FACE,{"disambiguationData":[TD([[makeQuery(id+"F0.imprint","IMPRINT",EDGE,{"disambiguationData":[TD([[subQ1,-1.0]])],"derivedFrom":subQ0}),1.0]])]});}
            var Q33;
            {var subQ2=sQuery(id+"F0.wireOp",EDGE,"E28");var subQ4=makeQuery(id+"F0.imprint","INTERSECT",VERTEX,{"derivedFrom":[sQuery(id+"F0.wireOp",EDGE,"E14"),subQ2]});Q33=makeQuery(id+"F0.imprint","IMPRINT",FACE,{"disambiguationData":[TD([[makeQuery(id+"F0.imprint","IMPRINT",EDGE,{"disambiguationData":[TD([[subQ4,1.0]])],"derivedFrom":subQ2}),-1.0]])]});}
            var Q34;
            {var subQ0=sQuery(id+"F0.wireOp",EDGE,"E28");var subQ1=sQuery(id+"F0.wireOp",EDGE,"E14");var subQ2=makeQuery(id+"F0.imprint","INTERSECT",VERTEX,{"derivedFrom":[subQ1,subQ0]});Q34=makeQuery(id+"F0.imprint","IMPRINT",FACE,{"disambiguationData":[TD([[makeQuery(id+"F0.imprint","IMPRINT",EDGE,{"disambiguationData":[TD([[subQ2,1.0]])],"derivedFrom":subQ1}),1.0]])]});}
            var Q35;
            {var subQ2=sQuery(id+"F0.wireOp",EDGE,"E14");var subQ4=sQuery(id+"F0.wireOp",EDGE,"E28");var subQ5=makeQuery(id+"F0.imprint","INTERSECT",VERTEX,{"derivedFrom":[subQ2,subQ4]});Q35=makeQuery(id+"F0.imprint","IMPRINT",FACE,{"disambiguationData":[TD([[makeQuery(id+"F0.imprint","IMPRINT",EDGE,{"disambiguationData":[TD([[subQ5,1.0]])],"derivedFrom":subQ2}),-1.0]])]});}
            var Q36;
            {var subQ0=sQuery(id+"F0.wireOp",EDGE,"E32");var subQ1=sQuery(id+"F0.wireOp",EDGE,"E16");var subQ2=makeQuery(id+"F0.imprint","INTERSECT",VERTEX,{"derivedFrom":[subQ1,subQ0]});Q36=makeQuery(id+"F0.imprint","IMPRINT",FACE,{"disambiguationData":[TD([[makeQuery(id+"F0.imprint","IMPRINT",EDGE,{"disambiguationData":[TD([[subQ2,-1.0]])],"derivedFrom":subQ0}),-1.0]])]});}
            var Q37;
            {var subQ0=sQuery(id+"F0.wireOp",EDGE,"E32");var subQ1=sQuery(id+"F0.wireOp",EDGE,"E16");var subQ2=makeQuery(id+"F0.imprint","INTERSECT",VERTEX,{"derivedFrom":[subQ1,subQ0]});Q37=makeQuery(id+"F0.imprint","IMPRINT",FACE,{"disambiguationData":[TD([[makeQuery(id+"F0.imprint","IMPRINT",EDGE,{"disambiguationData":[TD([[subQ2,-1.0]])],"derivedFrom":subQ0}),1.0]])]});}
            extrude(context, id + "F4", {"entities" : qUnion([Q0, Q1, Q2, Q3, Q4, Q5, Q6, Q7, Q8, Q9, Q10, Q11, Q12, Q13, Q14, Q15, Q16, Q17, Q18, Q19, Q20, Q21, Q22, Q23, Q24, Q25, Q26, Q27, Q28, Q29, Q30, Q31, Q32, Q33, Q34, Q35, Q36, Q37]), "operationType" : NewBodyOperationType.REMOVE, "depth" : 2 * mm});
        }
    });
